# Revit family: HUNTER_ACC-1200 Plastic Pedestal
name_source: partatom
category: Electrical Equipment
revit_build: Autodesk Revit 2017 (Build: 20160225_1515(x64)
units: mm (PartAtom-declared; Revit-internal decimal feet)

## family parameters
Always vertical = Yes
Cut with Voids When Loaded = No
OmniClass Number = 23.35.25.21
Panel Configuration = One Column
Part Type = Panelboard
Room Calculation Point = No
Round Connector Dimension = Use Diameter
Shared = Yes
Work Plane-Based = Yes

## types (1)
- ACC-1200-PP
    Assembly Code = D5090900
    Current = 2 A
    Decoders = Expandable Up to 99 with Decoders
    Default Elevation = 1219 mm
    Description = 12-Station base unit , Pedestal mounted controller, expandable to 42 stations, with Plastic Pedestal
    Expansion Module = A2M-600 (6 Stations plug-in) Expansion Module
    Input Voltage = 120 V
    Keynote = 328423.04
    Manufacturer = Hunter® Industries
    Model = ACC-1200-PP / ACC-1800-PP / ACC- 2400-PP / ACC-3000-PP / ACC-3600-PP / ACC-4200-PP
    Number of Sensor Inputs = 4+ Dedicated Flow Input
    Output Voltage = 24 V
    Panel Type = Modular
    Pedestal Material = Hunter® Plastic
    Pedestal_Depth = 430 mm
    Pedestal_Height = 990 mm
    Pedestal_Width = 610 mm
    Power = 240 VA
    Power Factor = 1
    Protection Rating = IP24
    Sensor Input = 4 + Flow
    Stations = 12 Stations base count expandable to 42 Stations
    Transformer Output = 24VAC, 4.0A
    Type Comments = Hunter's Flagship Controller
    Type Image = <None>
    URL = https://www.hunterindustries.com

## geometry (parser evidence)
native form markers: Sweep x5
no freeform markers — native parametric forms only
